FCSTD DOCUMENT  (FreeCAD 0.20R29410 (Git))
Label: ManipuladorAlámbrico (2)
License: All rights reserved
LicenseURL: http://en.wikipedia.org/wiki/All_rights_reserved
objects: Sketcher::SketchObject×1, PartDesign::Body×1
note: 2 computed .brp shape members not serialized (recipe doc carries the construction recipe); baked Part::Feature solids carry a one-line shape summary decoded from their .brp

FEATURE [Sketcher::SketchObject] Sketch
  FullyConstrained = false
  MapMode = 5
  Placement = pos=(0,0,0) rot=(1,0,0;1.5708rad)
  Support = -> [XZ_Plane]
  sketch-geometry (17):
    g0: LineSegment StartX=0 StartY=-3.6e-15 StartZ=0 EndX=-27.485 EndY=21.6697 EndZ=0
    g1: LineSegment StartX=-27.485 StartY=21.6697 StartZ=0 EndX=-144.408 EndY=145.076 EndZ=0
    g2: LineSegment StartX=-144.408 StartY=145.076 StartZ=0 EndX=-116.923 EndY=123.406 EndZ=0
    g3: LineSegment StartX=0 StartY=-3.6e-15 StartZ=0 EndX=-116.923 EndY=123.406 EndZ=0
    g4: LineSegment StartX=-116.923 StartY=123.406 StartZ=0 EndX=16.5754 EndY=18.153 EndZ=0
    g5: LineSegment StartX=-116.923 StartY=123.406 StartZ=0 EndX=-87.8834 EndY=142.943 EndZ=0
    g6: LineSegment StartX=-87.8834 StartY=142.943 StartZ=0 EndX=45.6151 EndY=37.6901 EndZ=0
    g7: LineSegment StartX=45.6151 StartY=37.6901 StartZ=0 EndX=16.5754 EndY=18.153 EndZ=0
    g8: LineSegment StartX=-87.8834 StartY=142.943 StartZ=0 EndX=-147.565 EndY=149.117 EndZ=0
    g9: LineSegment StartX=-116.923 StartY=123.406 StartZ=0 EndX=-147.565 EndY=149.117 EndZ=0
    g10: LineSegment StartX=-147.565 StartY=149.117 StartZ=0 EndX=-30.6418 EndY=25.7115 EndZ=0
    g11: LineSegment StartX=-30.6418 StartY=25.7115 StartZ=0 EndX=0 EndY=-7.1e-15 EndZ=0
    g12: LineSegment StartX=16.5754 StartY=18.153 StartZ=0 EndX=36.5754 EndY=18.153 EndZ=0
    g13: LineSegment StartX=16.5754 StartY=18.153 StartZ=0 EndX=26.5754 EndY=0.832493 EndZ=0
    g14: LineSegment StartX=36.5754 StartY=18.153 StartZ=0 EndX=26.5754 EndY=0.832493 EndZ=0
    g15: LineSegment StartX=0 StartY=-3.6e-15 StartZ=0 EndX=0 EndY=-51.8042 EndZ=0
    g16: LineSegment StartX=0 StartY=-51.8042 StartZ=0 EndX=159.214 EndY=-51.8042 EndZ=0
  constraints (44):
    c: Coincident(g0,g-1)
    c: Coincident(g1,g0)
    c: Coincident(g2,g1)
    c: Coincident(g3,g0)
    c: Coincident(g3,g2)
    c: Coincident(g4,g2)
    c: Coincident(g5,g2)
    c: Coincident(g6,g5)
    c: Coincident(g7,g6)
    c: Coincident(g7,g4)
    c: Coincident(g8,g5)
    c: Coincident(g9,g2)
    c: Coincident(g9,g8)
    c: Coincident(g10,g8)
    c: Coincident(g11,g10)
    c: Coincident(g11,g0)
    c: Equal(g2,g0)
    c: Equal(g4,g6)
    c: Equal(g5,g7)
    c: Equal(g3,g1)
    c: Equal(g3,g10)
    c: Equal(g9,g11)
    c: Parallel(g2,g4)
    c: Distance(g3) = 170  'LargoParalelepipedo1'
    c: Distance(g2) = 35  'AnchoParalelepipedo1-1'
    c: Distance(g9) = 40  'AnchoParalelepipedo1-2'
    c: Distance(g4) = 170  'LargoParalelepipedo2'
    c: Distance(g7) = 35  'AnchoParalelepipedo2'
    c: Distance(g8) = 60  'LargoCodo'
    c: Angle(g-1,g11) = 2.44346  'AnguloBase'
    c: Coincident(g12,g4)
    c: Distance(g12) = 20
    c: Coincident(g13,g4)
    c: Coincident(g14,g12)
    c: Coincident(g14,g13)
    c: Equal(g12,g14)
    c: Equal(g13,g12)
    c: Coincident(g15,g0)
    c: Vertical(g15)
    c: Coincident(g16,g15)
    c: Horizontal(g16)
    c: Block(g15)
    c: Block(g16)
    c: Horizontal(g12)
FEATURE [PartDesign::Body] Body
  Group = -> [Sketch]
  Origin = -> Origin
